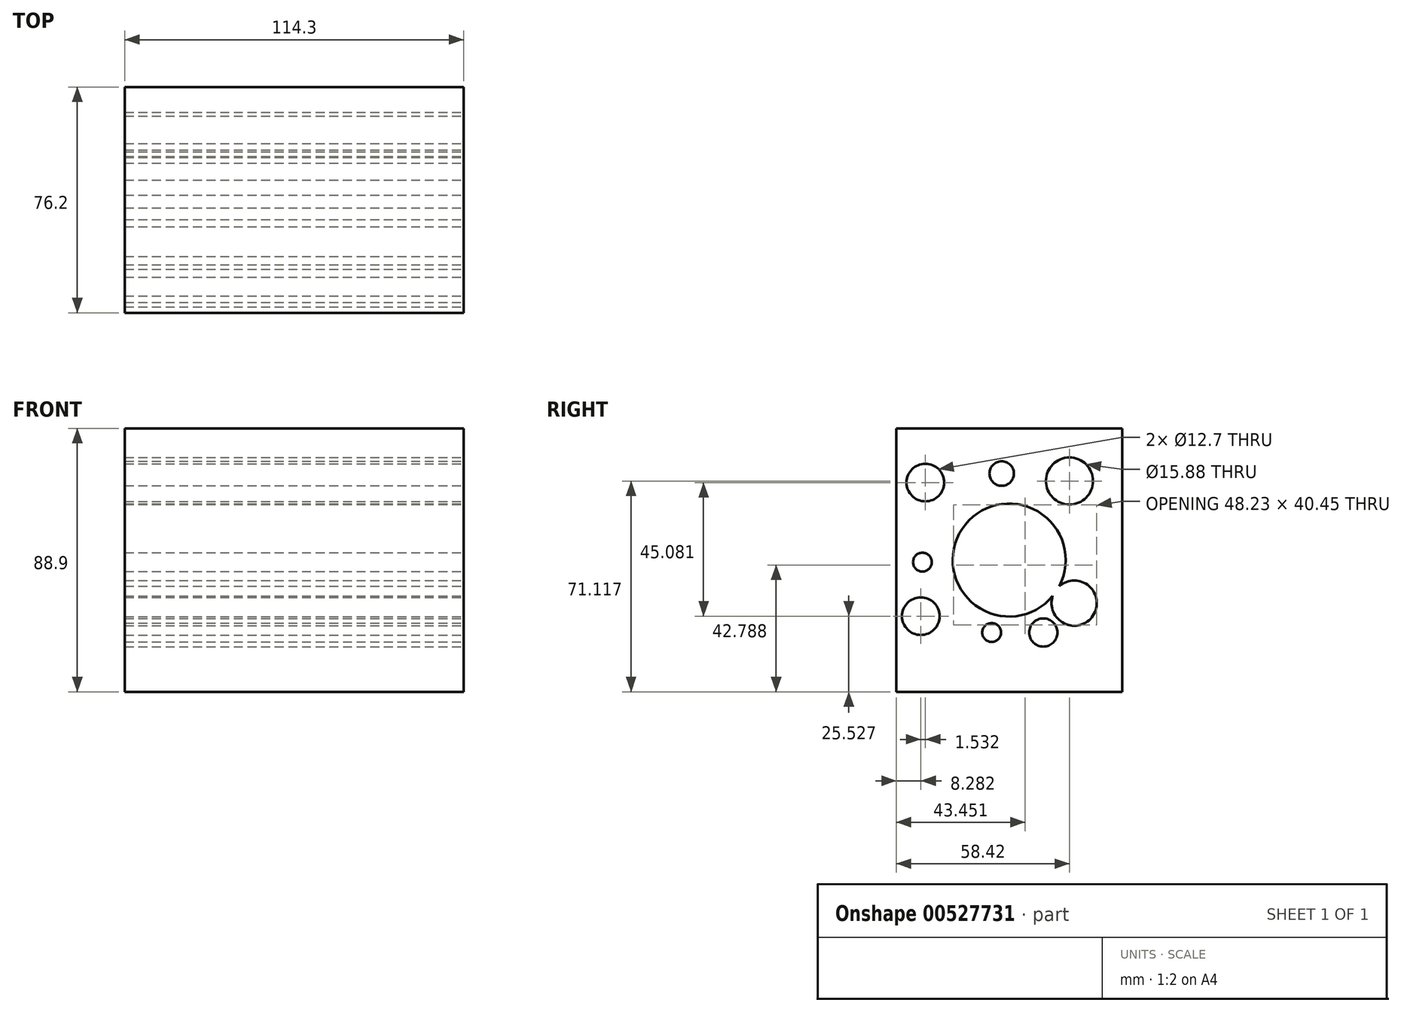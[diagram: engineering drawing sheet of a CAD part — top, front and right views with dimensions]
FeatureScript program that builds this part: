
annotation { "Feature Type Name" : "Feature", "Feature Type Description" : "" }
export const myFeature = defineFeature(function(context is Context, id is Id, definition is map)
    precondition{}
    {
        {
            var Q0;
            Q0=qCreatedBy(makeId("Front.planeOp"),FACE);
            var sketch = newSketch(context, id + "F0", { "sketchPlane" : qUnion([Q0])});
            skLineSegment(sketch, "E0.bottom", {"start": v(-53.79, 39.22) * mm, "end": v(60.51, 39.22) * mm});
            skLineSegment(sketch, "E0.top", {"start": v(-53.79, -49.68) * mm, "end": v(60.51, -49.68) * mm});
            skLineSegment(sketch, "E0.left", {"start": v(-53.79, 39.22) * mm, "end": v(-53.79, -49.68) * mm});
            skLineSegment(sketch, "E0.right", {"start": v(60.51, 39.22) * mm, "end": v(60.51, -49.68) * mm});
            skSolve(sketch);
        }
        {
            var Q0;
            Q0 = qSketchRegion(id + "F0", true);
            extrude(context, id + "F1", {"entities" : qUnion([Q0]), "depth" : 76.2 * mm, "offsetDistance" : 25.4 * mm});
        }
        {
            var Q0;
            Q0=makeQuery(id+"F1.opExtrude","SWEPT_FACE",FACE,{"disambiguationData":[OSD([sQuery(id+"F0.wireOp",EDGE,"E0.right")])]});
            var sketch = newSketch(context, id + "F2", { "sketchPlane" : qUnion([Q0])});
            skCircle(sketch, "E1", {"center": v(-38.1, -5.23) * mm, "radius": 19.05 * mm});
            skCircle(sketch, "E2", {"center": v(-66.39, 20.93) * mm, "radius": 6.35 * mm});
            skCircle(sketch, "E3", {"center": v(-17.78, 21.44) * mm, "radius": 7.94 * mm});
            skCircle(sketch, "E4", {"center": v(-16.19, -19.76) * mm, "radius": 7.62 * mm});
            skCircle(sketch, "E5", {"center": v(-67.92, -24.15) * mm, "radius": 6.35 * mm});
            skCircle(sketch, "E6", {"center": v(-67.37, -5.92) * mm, "radius": 3.18 * mm});
            skCircle(sketch, "E7", {"center": v(-44.02, -29.68) * mm, "radius": 3.18 * mm});
            skCircle(sketch, "E8", {"center": v(-40.64, 23.98) * mm, "radius": 4.13 * mm});
            skCircle(sketch, "E9", {"center": v(-26.6, -29.68) * mm, "radius": 4.76 * mm});
            skSolve(sketch);
        }
        {
            var Q0;
            Q0 = qSketchRegion(id + "F2", true);
            var Q1;
            Q1=makeQuery(id+"F1.opExtrude","SWEPT_FACE",FACE,{"disambiguationData":[OSD([sQuery(id+"F0.wireOp",EDGE,"E0.left")])]});
            extrude(context, id + "F3", {"entities" : qUnion([Q0]), "operationType" : NewBodyOperationType.REMOVE, "endBound" : BoundingType.UP_TO_SURFACE, "oppositeDirection" : true, "depth" : 25.4 * mm, "endBoundEntityFace" : qUnion([Q1]), "offsetDistance" : 25.4 * mm});
        }
    });
